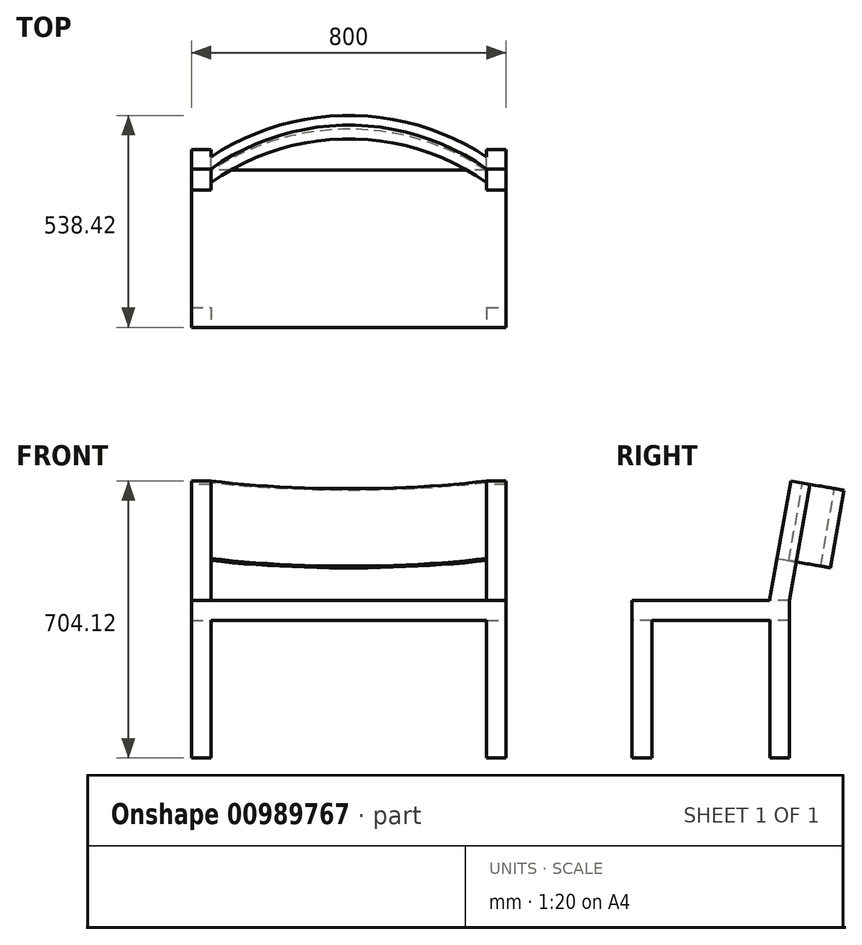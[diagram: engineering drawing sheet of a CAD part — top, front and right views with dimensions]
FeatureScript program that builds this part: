
annotation { "Feature Type Name" : "Feature", "Feature Type Description" : "" }
export const myFeature = defineFeature(function(context is Context, id is Id, definition is map)
    precondition{}
    {
        {
            var Q0;
            Q0=qCreatedBy(makeId("Top.planeOp"),FACE);
            var sketch = newSketch(context, id + "F0", { "sketchPlane" : qUnion([Q0])});
            skLineSegment(sketch, "E0.bottom", {"start": v(400, 200) * mm, "end": v(-400, 200) * mm});
            skLineSegment(sketch, "E0.top", {"start": v(400, -200) * mm, "end": v(-400, -200) * mm});
            skLineSegment(sketch, "E0.left", {"start": v(400, 200) * mm, "end": v(400, -200) * mm});
            skLineSegment(sketch, "E0.right", {"start": v(-400, 200) * mm, "end": v(-400, -200) * mm});
            skPoint(sketch, "E0.middle", {"position": v(0, 0) * mm});
            skSolve(sketch);
        }
        {
            var Q0;
            Q0=makeQuery(id+"F0.imprint","IMPRINT",FACE,{"disambiguationData":[TD([[makeQuery(id+"F0.imprint","IMPRINT",EDGE,{"derivedFrom":sQuery(id+"F0.wireOp",EDGE,"E0.bottom")}),1.0]])]});
            extrude(context, id + "F1", {"entities" : qUnion([Q0]), "depth" : 400 * mm, "offsetDistance" : 25 * mm});
        }
        {
            var Q0;
            Q0=makeQuery(id+"F1.opExtrude","SWEPT_FACE",FACE,{"disambiguationData":[OSD([sQuery(id+"F0.wireOp",EDGE,"E0.left")])]});
            var sketch = newSketch(context, id + "F2", { "sketchPlane" : qUnion([Q0])});
            skLineSegment(sketch, "E1.bottom", {"start": v(-150, 0) * mm, "end": v(150, 0) * mm});
            skLineSegment(sketch, "E1.top", {"start": v(-150, 350) * mm, "end": v(150, 350) * mm});
            skLineSegment(sketch, "E1.left", {"start": v(-150, 0) * mm, "end": v(-150, 350) * mm});
            skLineSegment(sketch, "E1.right", {"start": v(150, 0) * mm, "end": v(150, 350) * mm});
            skSolve(sketch);
        }
        {
            var Q0;
            Q0=makeQuery(id+"F2.imprint","IMPRINT",FACE,{"disambiguationData":[TD([[makeQuery(id+"F2.imprint","IMPRINT",EDGE,{"derivedFrom":sQuery(id+"F2.wireOp",EDGE,"E1.bottom")}),-1.0]])]});
            extrude(context, id + "F3", {"entities" : qUnion([Q0]), "operationType" : NewBodyOperationType.REMOVE, "endBound" : BoundingType.THROUGH_ALL, "oppositeDirection" : true, "depth" : 25 * mm, "offsetDistance" : 25 * mm});
        }
        {
            var Q0;
            Q0=makeQuery(id+"F1.opExtrude","SWEPT_FACE",FACE,{"disambiguationData":[OSD([sQuery(id+"F0.wireOp",EDGE,"E0.top")])]});
            var sketch = newSketch(context, id + "F4", { "sketchPlane" : qUnion([Q0])});
            skLineSegment(sketch, "E2.bottom", {"start": v(-350, 0) * mm, "end": v(350, 0) * mm});
            skLineSegment(sketch, "E2.top", {"start": v(-350, 350) * mm, "end": v(350, 350) * mm});
            skLineSegment(sketch, "E2.left", {"start": v(-350, 0) * mm, "end": v(-350, 350) * mm});
            skLineSegment(sketch, "E2.right", {"start": v(350, 0) * mm, "end": v(350, 350) * mm});
            skSolve(sketch);
        }
        {
            var Q0;
            Q0=makeQuery(id+"F4.imprint","IMPRINT",FACE,{"disambiguationData":[TD([[makeQuery(id+"F4.imprint","IMPRINT",EDGE,{"derivedFrom":sQuery(id+"F4.wireOp",EDGE,"E2.bottom")}),-1.0]])]});
            extrude(context, id + "F5", {"entities" : qUnion([Q0]), "operationType" : NewBodyOperationType.REMOVE, "endBound" : BoundingType.THROUGH_ALL, "oppositeDirection" : true, "depth" : 25 * mm, "offsetDistance" : 25 * mm});
        }
        {
            var Q0;
            Q0=makeQuery(id+"F1.opExtrude","SWEPT_FACE",FACE,{"disambiguationData":[OSD([sQuery(id+"F0.wireOp",EDGE,"E0.bottom")])]});
            var Q1;
            Q1=makeQuery(id+"F1.opExtrude","CAP_VERTEX",VERTEX,{"disambiguationData":[OSD([sQuery(id+"F0.wireOp",EDGE,"E0.bottom"),sQuery(id+"F0.wireOp",EDGE,"E0.right")])],"isStart":false});
            cPlane(context, id + "F6", {"entities" : qUnion([Q0, Q1]), "cplaneType" : CPlaneType.PLANE_POINT, "offset" : 25 * mm, "width" : 150 * mm, "height" : 150 * mm});
        }
        {
            var Q0;
            Q0=makeQuery(id+"F1.opExtrude","CAP_EDGE",EDGE,{"disambiguationData":[OSD([sQuery(id+"F0.wireOp",EDGE,"E0.bottom")])],"isStart":false});
            var Q1;
            Q1=qCreatedBy(id+"F6.planeOp",FACE);
            cPlane(context, id + "F7", {"entities" : qUnion([Q0, Q1]), "cplaneType" : CPlaneType.LINE_ANGLE, "offset" : 25 * mm, "angle" : 10 * degree, "width" : 150 * mm, "height" : 150 * mm});
        }
        {
            var Q0;
            Q0=qCreatedBy(id+"F7.planeOp",FACE);
            var sketch = newSketch(context, id + "F8", { "sketchPlane" : qUnion([Q0])});
            skLineSegment(sketch, "E3.bottom", {"start": v(400, 428.65) * mm, "end": v(-400, 428.65) * mm});
            skLineSegment(sketch, "E3.top", {"start": v(400, 728.65) * mm, "end": v(-400, 728.65) * mm});
            skLineSegment(sketch, "E3.left", {"start": v(400, 428.65) * mm, "end": v(400, 728.65) * mm});
            skLineSegment(sketch, "E3.right", {"start": v(-400, 428.65) * mm, "end": v(-400, 728.65) * mm});
            skSolve(sketch);
        }
        {
            var Q0;
            Q0=makeQuery(id+"F8.imprint","IMPRINT",FACE,{"disambiguationData":[TD([[makeQuery(id+"F8.imprint","IMPRINT",EDGE,{"derivedFrom":sQuery(id+"F8.wireOp",EDGE,"E3.bottom")}),-1.0]])]});
            extrude(context, id + "F9", {"entities" : qUnion([Q0]), "depth" : 50 * mm, "offsetDistance" : 25 * mm});
        }
        {
            var Q0;
            Q0=makeQuery(id+"F9.opExtrude","CAP_FACE",FACE,{"disambiguationData":[OSD([sQuery(id+"F8.wireOp",EDGE,"E3.bottom"),sQuery(id+"F8.wireOp",EDGE,"E3.top"),sQuery(id+"F8.wireOp",EDGE,"E3.left"),sQuery(id+"F8.wireOp",EDGE,"E3.right")])],"isStart":true});
            var sketch = newSketch(context, id + "F10", { "sketchPlane" : qUnion([Q0])});
            skLineSegment(sketch, "E4.bottom", {"start": v(-350, 428.65) * mm, "end": v(350, 428.65) * mm});
            skLineSegment(sketch, "E4.top", {"start": v(-350, 728.65) * mm, "end": v(350, 728.65) * mm});
            skLineSegment(sketch, "E4.left", {"start": v(-350, 428.65) * mm, "end": v(-350, 728.65) * mm});
            skLineSegment(sketch, "E4.right", {"start": v(350, 428.65) * mm, "end": v(350, 728.65) * mm});
            skSolve(sketch);
        }
        {
            var Q0;
            Q0=makeQuery(id+"F10.imprint","IMPRINT",FACE,{"disambiguationData":[TD([[makeQuery(id+"F10.imprint","IMPRINT",EDGE,{"derivedFrom":sQuery(id+"F10.wireOp",EDGE,"E4.bottom")}),1.0]])]});
            extrude(context, id + "F11", {"entities" : qUnion([Q0]), "operationType" : NewBodyOperationType.REMOVE, "endBound" : BoundingType.THROUGH_ALL, "oppositeDirection" : true, "depth" : 25 * mm, "offsetDistance" : 25 * mm});
        }
        {
            var Q0;
            {var subQ0=sQuery(id+"F8.wireOp",EDGE,"E3.right");var subQ3=sQuery(id+"F8.wireOp",EDGE,"E3.bottom");Q0=makeQuery(id+"F11.boolean.opBoolean","SPLIT",FACE,{"disambiguationData":[TD([makeQuery(id+"F9.opExtrude","SWEPT_FACE",FACE,{"disambiguationData":[OSD([subQ0])]})])],"derivedFrom":makeQuery(id+"F9.opExtrude","SWEPT_FACE",FACE,{"disambiguationData":[OSD([subQ3])]})});}
            extrude(context, id + "F12", {"entities" : qUnion([Q0]), "operationType" : NewBodyOperationType.ADD, "endBound" : BoundingType.UP_TO_NEXT, "depth" : 25 * mm, "offsetDistance" : 25 * mm});
        }
        {
            var Q0;
            {var subQ1=sQuery(id+"F8.wireOp",EDGE,"E3.left");var subQ3=sQuery(id+"F8.wireOp",EDGE,"E3.bottom");Q0=makeQuery(id+"F11.boolean.opBoolean","SPLIT",FACE,{"disambiguationData":[TD([makeQuery(id+"F9.opExtrude","SWEPT_FACE",FACE,{"disambiguationData":[OSD([subQ1])]})])],"derivedFrom":makeQuery(id+"F9.opExtrude","SWEPT_FACE",FACE,{"disambiguationData":[OSD([subQ3])]})});}
            extrude(context, id + "F13", {"entities" : qUnion([Q0]), "operationType" : NewBodyOperationType.ADD, "endBound" : BoundingType.UP_TO_NEXT, "depth" : 25 * mm, "offsetDistance" : 25 * mm});
        }
        {
            var Q0;
            {var subQ1=sQuery(id+"F8.wireOp",EDGE,"E3.left");var subQ2=sQuery(id+"F8.wireOp",EDGE,"E3.top");Q0=makeQuery(id+"F11.boolean.opBoolean","SPLIT",FACE,{"disambiguationData":[TD([makeQuery(id+"F9.opExtrude","SWEPT_FACE",FACE,{"disambiguationData":[OSD([subQ1])]})])],"derivedFrom":makeQuery(id+"F9.opExtrude","SWEPT_FACE",FACE,{"disambiguationData":[OSD([subQ2])]})});}
            var sketch = newSketch(context, id + "F14", { "sketchPlane" : qUnion([Q0])});
            skArc(sketch, "E5", {"start": v(350, 77.5) * mm, "mid": v(0, 190.16) * mm, "end": v(-350, 77.5) * mm});
            skArc(sketch, "E6.0", {"start": v(364.58, 97.8) * mm, "mid": v(0, 215.16) * mm, "end": v(-364.58, 97.8) * mm});
            skLineSegment(sketch, "E7", {"start": v(364.58, 97.8) * mm, "end": v(350, 77.5) * mm});
            skLineSegment(sketch, "E8", {"start": v(-364.58, 97.8) * mm, "end": v(-350, 77.5) * mm});
            skSolve(sketch);
        }
        {
            var Q0;
            {var subQ0=sQuery(id+"F14.wireOp",EDGE,"E5");Q0=makeQuery(id+"F14.imprint","IMPRINT",FACE,{"disambiguationData":[TD([[makeQuery(id+"F14.imprint","IMPRINT",EDGE,{"derivedFrom":subQ0}),-1.0]])]});}
            extrude(context, id + "F15", {"entities" : qUnion([Q0]), "operationType" : NewBodyOperationType.ADD, "oppositeDirection" : true, "depth" : 200 * mm, "offsetDistance" : 25 * mm});
        }
        {
            var Q0;
            Q0=makeQuery(id+"F4.imprint","IMPRINT",FACE,{"disambiguationData":[TD([[makeQuery(id+"F4.imprint","IMPRINT",EDGE,{"derivedFrom":sQuery(id+"F4.wireOp",EDGE,"E2.top")}),1.0]])]});
            cPlane(context, id + "F16", {"entities" : qUnion([Q0]), "cplaneType" : CPlaneType.OFFSET, "offset" : 25 * mm, "width" : 150 * mm, "height" : 150 * mm});
        }
    });
